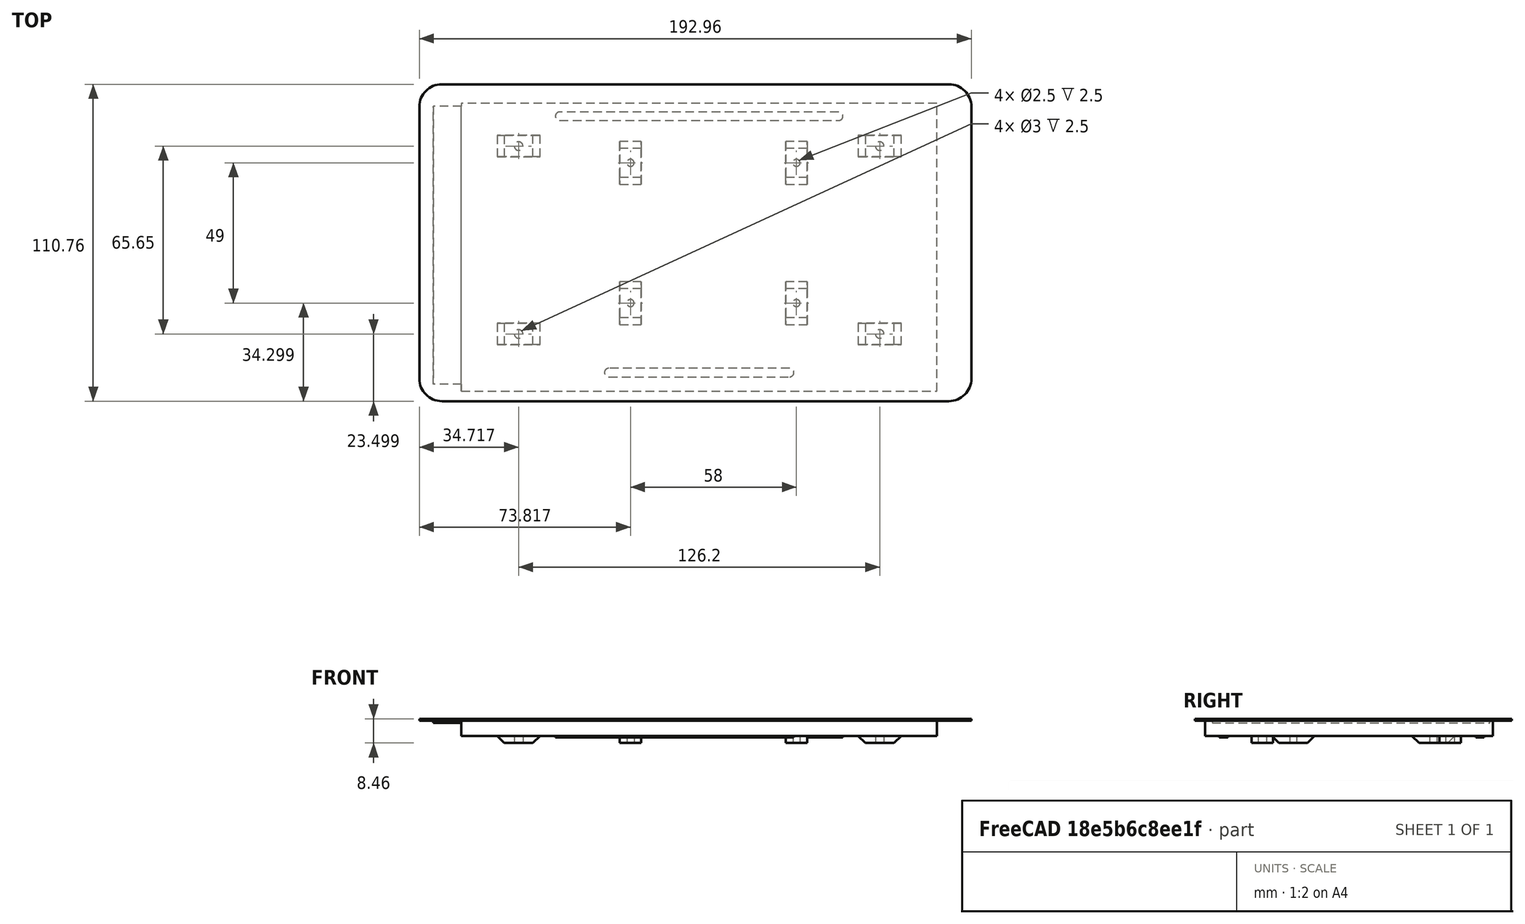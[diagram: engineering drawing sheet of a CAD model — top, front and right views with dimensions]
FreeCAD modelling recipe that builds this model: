
FCSTD DOCUMENT  (FreeCAD 0.18R15619 (Git))
Label: touchscreen
License: All rights reserved
LicenseURL: http://en.wikipedia.org/wiki/All_rights_reserved
objects: Part::Feature×3, Part::Fuse×2
note: 5 computed .brp shape members not serialized (recipe doc carries the construction recipe); baked Part::Feature solids carry a one-line shape summary decoded from their .brp

FEATURE [Part::Feature] Part__Feature  label="Display Lens"
  Placement = pos=(16.7487,-7.44536,1.09301) rot=(0,0,-1;0rad)
  shape: bbox 193 x 110.8 x 0.7 mm, 14 faces (baked)
FEATURE [Part::Feature] Part__Feature001  label="Display Glass"
  Placement = pos=(16.7487,-7.44536,1.09301) rot=(0,0,-1;0rad)
  shape: bbox 154.9 x 86.72 x 0.7 mm, 6 faces (baked)
FEATURE [Part::Feature] Part__Feature002  label="Display Controller"
  Placement = pos=(18.0874,-9.03115,-4.86699) rot=(0,0,-1;0rad)
  shape: bbox 176 x 100.6 x 7.76 mm, 76 faces (baked)
FEATURE [Part::Fuse] Fusion
  Base = -> Part__Feature
  Tool = -> Part__Feature001
FEATURE [Part::Fuse] Fusion001
  Base = -> Fusion
  Tool = -> Part__Feature002
